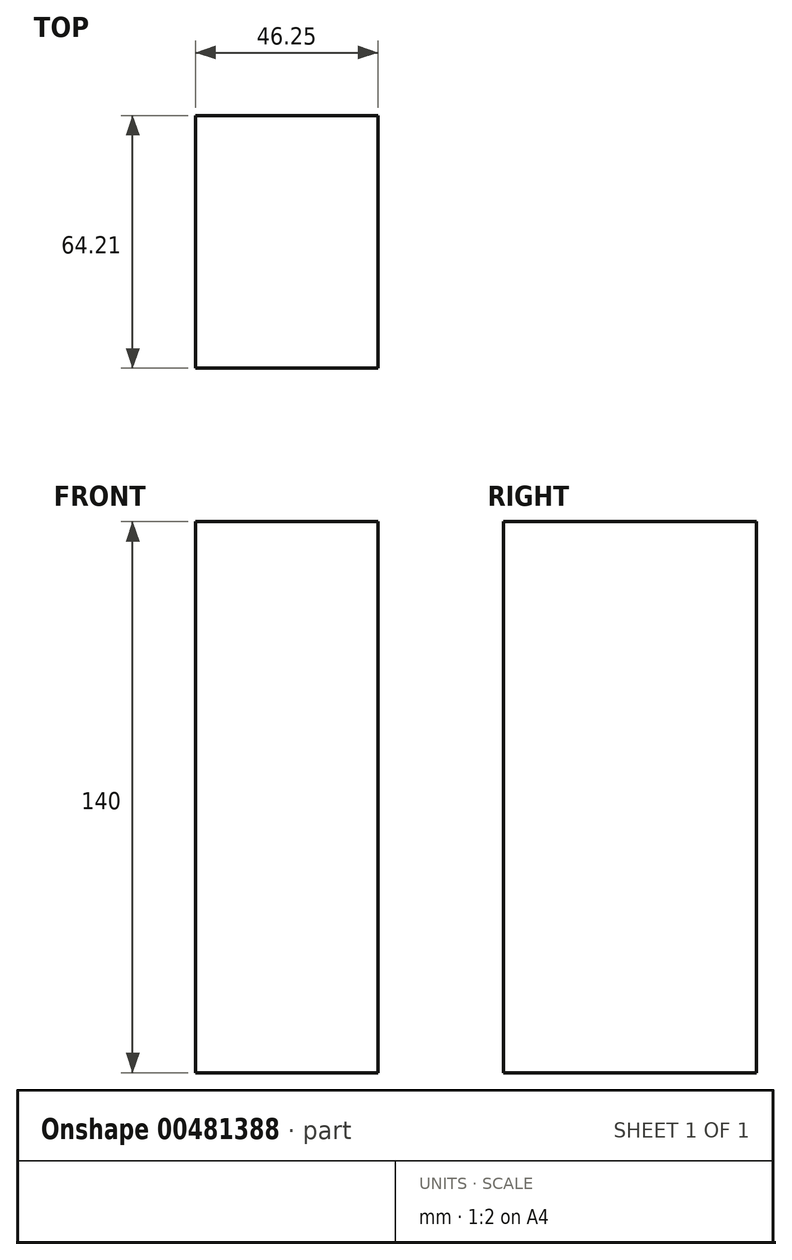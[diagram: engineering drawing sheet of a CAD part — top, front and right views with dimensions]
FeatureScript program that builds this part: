
annotation { "Feature Type Name" : "Feature", "Feature Type Description" : "" }
export const myFeature = defineFeature(function(context is Context, id is Id, definition is map)
    precondition{}
    {
        {
            var Q0;
            Q0=qCreatedBy(makeId("Top.planeOp"),FACE);
            var sketch = newSketch(context, id + "F0", { "sketchPlane" : qUnion([Q0])});
            skLineSegment(sketch, "E0.bottom", {"start": v(-23.9, 21.42) * mm, "end": v(22.34, 21.42) * mm});
            skLineSegment(sketch, "E0.top", {"start": v(-23.9, -42.8) * mm, "end": v(22.34, -42.8) * mm});
            skLineSegment(sketch, "E0.left", {"start": v(-23.9, 21.42) * mm, "end": v(-23.9, -42.8) * mm});
            skLineSegment(sketch, "E0.right", {"start": v(22.34, 21.42) * mm, "end": v(22.34, -42.8) * mm});
            skSolve(sketch);
        }
        {
            var Q0;
            Q0 = qSketchRegion(id + "F0", true);
            extrude(context, id + "F1", {"entities" : qUnion([Q0]), "depth" : 140 * mm, "offsetDistance" : 25 * mm});
        }
    });
